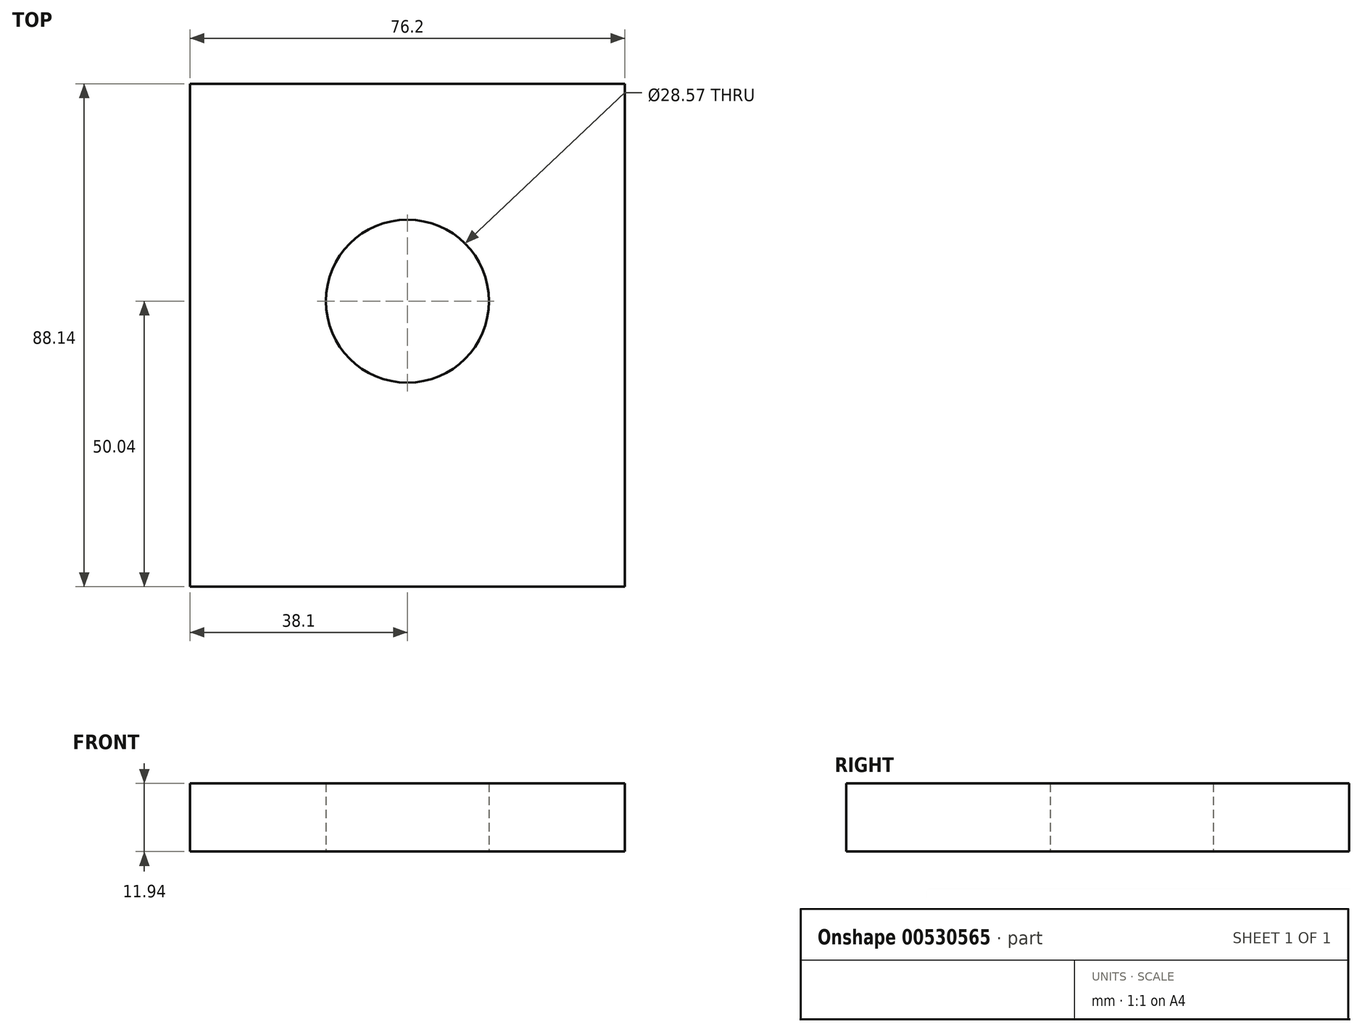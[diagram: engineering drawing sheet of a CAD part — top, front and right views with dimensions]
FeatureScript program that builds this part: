
annotation { "Feature Type Name" : "Feature", "Feature Type Description" : "" }
export const myFeature = defineFeature(function(context is Context, id is Id, definition is map)
    precondition{}
    {
        {
            var Q0;
            Q0=qCreatedBy(makeId("Top.planeOp"),FACE);
            var sketch = newSketch(context, id + "F0", { "sketchPlane" : qUnion([Q0])});
            skLineSegment(sketch, "E0.bottom", {"start": v(0, 0) * mm, "end": v(76.2, 0) * mm});
            skLineSegment(sketch, "E0.top", {"start": v(0, -88.14) * mm, "end": v(76.2, -88.14) * mm});
            skLineSegment(sketch, "E0.left", {"start": v(0, 0) * mm, "end": v(0, -88.14) * mm});
            skLineSegment(sketch, "E0.right", {"start": v(76.2, 0) * mm, "end": v(76.2, -88.14) * mm});
            skCircle(sketch, "E1", {"center": v(38.1, -38.1) * mm, "radius": 14.29 * mm});
            skSolve(sketch);
        }
        {
            var Q0;
            Q0 = qSketchRegion(id + "F0", true);
            extrude(context, id + "F1", {"entities" : qUnion([Q0]), "depth" : 11.94 * mm, "offsetDistance" : 25.4 * mm});
        }
    });
